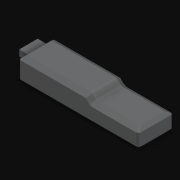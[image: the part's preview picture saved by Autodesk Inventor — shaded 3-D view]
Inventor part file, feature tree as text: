
AUTODESK INVENTOR PART (.ipt)
format: ipt  version: 2021 (Build 250183000, 183)  size: 223,744 bytes
history: native  units: in
note: dims shown in document units (in); Inventor stores cm internally (conversion verified against a paired STEP export)
features: chamfer x8, extrude x2, fillet x2, sketch x2
ambient origin geometry x8: Origin, YZ Plane, XZ Plane, XY Plane, X Axis, Y Axis, Z Axis, Center Point
bodies: Solid1 (feature_tree)
feature tree (14):
  extrude  "Extrusion1"  Depth=1.197in
  fillet  "Fillet1"  Radius=2.656in
  chamfer  "Chamfer1"  Distance=2.539in
  chamfer  "Chamfer3"  Distance=0.183in
  chamfer  "Chamfer2"  Distance=0.248in
  chamfer  "Chamfer4"  Distance=1.828in
  chamfer  "Chamfer5"  Distance=0.223in
  chamfer  "Chamfer6"  Distance=0.181in Angle=45.0deg
  chamfer  "Chamfer7"  Distance=0.161in Angle=45.0deg
  chamfer  "Chamfer8"  Distance=0.161in Angle=45.0deg
  fillet  "Fillet2"  Radius=0.161in
  extrude  "Extrusion2"  Depth=0.625in TaperAngle=45.0deg
  sketch  "Sketch1"  dims[d0=6.317in d1=1.197in d4=2.656in]
  sketch  "Sketch2"  dims[d5=0.065in d8=2.539in d9=0.183in d10=0.248in d12=1.828in d13=0.0in d14=0.223in d15=0.181in d16=0.161in d17=45.0deg d18=0.161in d19=0.254in d20=45.0deg d21=0.161in d22=0.254in d23=45.0deg d24=0.161in d25=0.181in d26=45.0deg d27=0.135in d28=0.158in d29=45.0deg d30=0.153in d31=0.249in d32=45.0deg d33=0.158in d34=0.135in d35=45.0deg d36=0.153in d37=0.249in d38=45.0deg d39=0.125in d40=0.3483in d41=0.3238in d42=0.9718in d43=0.1531in d44=0.3104in d45=0.3238in d46=0.9718in d47=0.3104in d48=0.1531in d49=0.3483in d50=0.3131in d51=0.3131in d52=0.347in d53=0.203in d54=0.625in d55=0.0in]
